# Revit family: NBS_Allermuir_OffcTbls_Oran-en-us
name_source: partatom
category: Furniture
revit_build: Autodesk Revit 2016 (Build: 20151007_0715(x64)
units: mm (PartAtom-declared; Revit-internal decimal feet)

## family parameters
Always vertical = Yes
Cut with Voids When Loaded = No
Room Calculation Point = No
Shared = No
Work Plane-Based = No

## types (1)
- ORAT2929
    AssetType = Moveable
    BIMObjectName = NBS_Allermuir_OfficeTables_Oran_ORAT2929-US
    Category = Pr_40_50_21_60:Office tables
    ColourOptions = Matt black, tusk grey
    Description = Coffee table
    DurationUnit = year
    ExpectedLife = 10
    ExposedEdges = Stained to match laminate top
    Features = Laminate faced MDF core top available in matt black or tusk grey, 6 mm visible edge profile is stained to match the laminate top, cast aluminum legs and aluminum perimeter frame finished in black powder coat, plastic glides, aluminum frame available in tusk grey powder coat
    FrameMaterial = NBS_Concept
    FramesColour = Black, tusk grey
    FramesSizes = 0 "
    FramesSupports = Cast aluminium legs, powder coated
    Functions = Meeting room
    IfcExportAs = IfcFurnitureType
    IfcExportType = TABLE
    IntegralAccessories = Plastic glides
    IsBuiltIn = No
    ManufacturerName = Allermuir
    ManufacturerURL = http://www.thesenatorgroup.com
    Material = Laminate faced MDF
    ModelNumber = ORAT2929
    ModelReference = Oran tables
    NBSCertification = www.nationalbimlibrary.com/cert/a0fvnwvg
    NBSDescription = Office tables
    NBSReference = 45-35-20/340
    Name = OfficeTables_Oran_ORAT2929_Allermuir
    NominalDepth = 29 "
    NominalHeight = 10 "
    NominalLength = 29 "
    NominalWidth = 29 "
    NumberOfChairs = 0
    OmniClassCode = 22-12 51 23
    OmniClassTitle = Office Tables
    OmniClassVersion = Table 22 2012-05-16
    Size = 29 x 29 x 9.5"
    Status = UNSET
    Uniclass2015Code = Pr_40_50_21_60
    Uniclass2015Title = Office tables
    Uniclass2015Version = Products v1.9
    Version = 1
    WarrantyDescription = Allermuir warrant that its manufactured products are free from manufacturing defects - in materials or workmanship - for a period of ten (10) years. Allermuir will repair, or replace (at Allermuir's sole discretion) with comparable free of charge materials / components, any product / component which fails under normal use in a single shift environment, as a result of a defect in the materials and/ or workmanship
    WarrantyDurationParts = 10
    WarrantyDurationUnit = year
    WorksurfaceArea = 0 m²
    WorktopMaterial = NBS_Concept

## geometry (parser evidence)
native form markers: Sweep x8
no freeform markers — native parametric forms only
